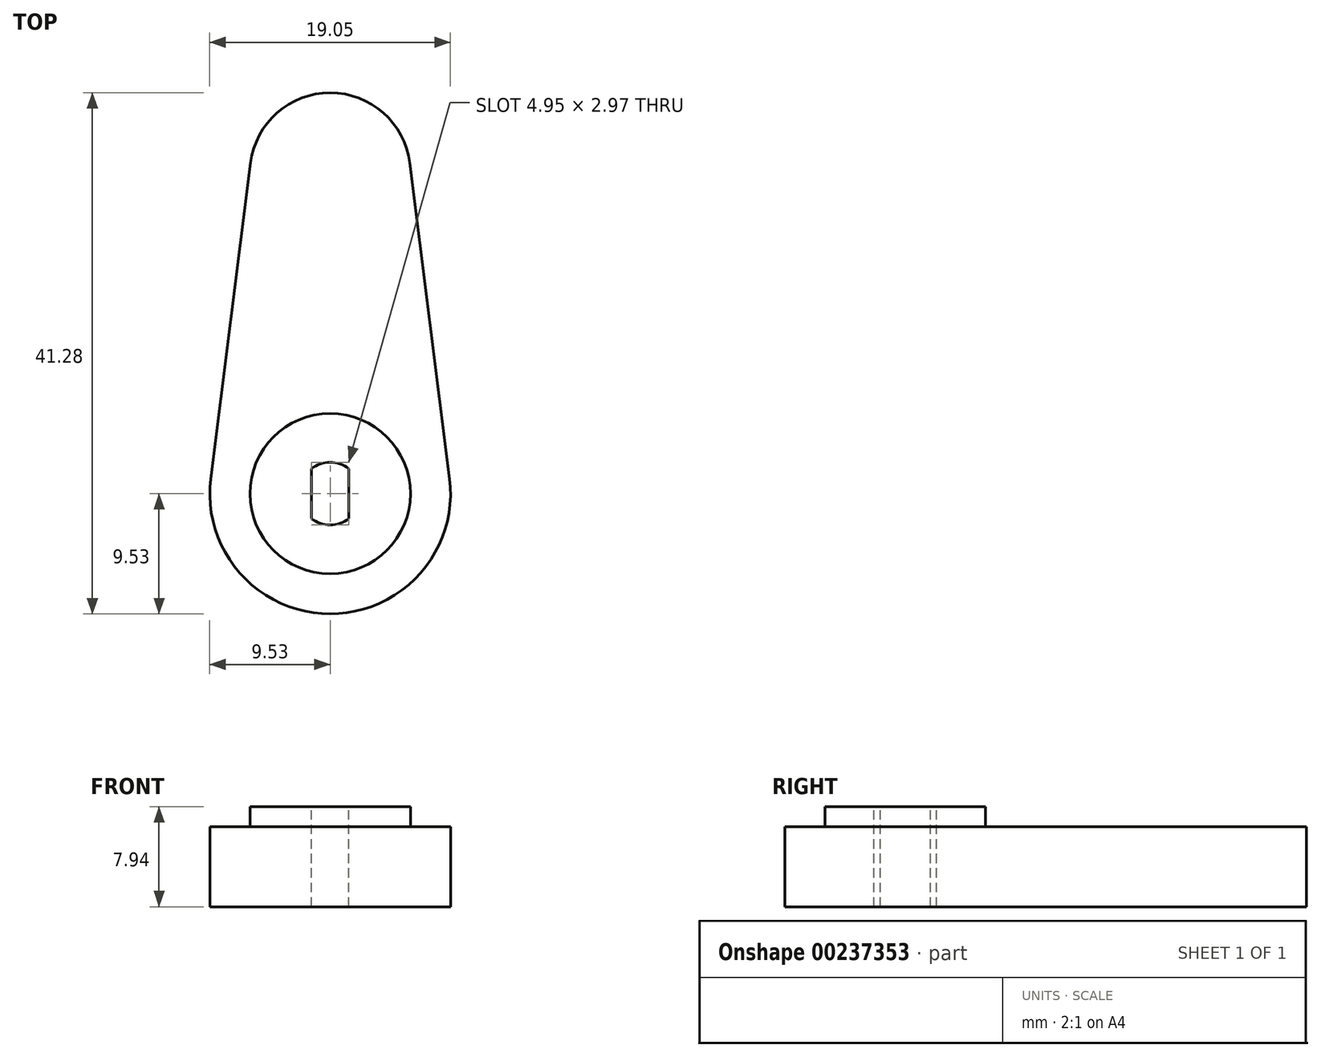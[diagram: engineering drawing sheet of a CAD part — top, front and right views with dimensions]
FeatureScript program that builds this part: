
annotation { "Feature Type Name" : "Feature", "Feature Type Description" : "" }
export const myFeature = defineFeature(function(context is Context, id is Id, definition is map)
    precondition{}
    {
        {
            var Q0;
            Q0=qCreatedBy(makeId("Top.planeOp"),FACE);
            var sketch = newSketch(context, id + "F0", { "sketchPlane" : qUnion([Q0])});
            skArc(sketch, "E0", {"start": v(-1.49, -1.98) * mm, "mid": v(0, -2.48) * mm, "end": v(1.49, -1.98) * mm});
            skLineSegment(sketch, "E1", {"start": v(-1.49, -1.98) * mm, "end": v(-1.49, 1.98) * mm});
            skLineSegment(sketch, "E2", {"start": v(1.49, -1.98) * mm, "end": v(1.49, 1.98) * mm});
            skArc(sketch, "E3.trimOffspring", {"start": v(1.49, 1.98) * mm, "mid": v(0, 2.48) * mm, "end": v(-1.49, 1.98) * mm});
            skPoint(sketch, "E4.orphan", {"position": v(1.49, 5.26) * mm});
            skPoint(sketch, "E5.orphan", {"position": v(-1.49, 5.26) * mm});
            skPoint(sketch, "E6.orphan", {"position": v(-1.49, -3.31) * mm});
            skCircle(sketch, "E7", {"center": v(0, 0) * mm, "radius": 6.35 * mm});
            skSolve(sketch);
        }
        {
            var Q0;
            Q0=makeQuery(id+"F0.imprint","IMPRINT",FACE,{"disambiguationData":[TD([[makeQuery(id+"F0.imprint","IMPRINT",EDGE,{"derivedFrom":sQuery(id+"F0.wireOp",EDGE,"E0")}),-1.0]])]});
            extrude(context, id + "F1", {"entities" : qUnion([Q0]), "oppositeDirection" : true, "depth" : 1.59 * mm});
        }
        {
            var Q0;
            Q0=makeQuery(id+"F1.opExtrude","CAP_FACE",FACE,{"disambiguationData":[OSD([sQuery(id+"F0.wireOp",EDGE,"E0"),sQuery(id+"F0.wireOp",EDGE,"E1"),sQuery(id+"F0.wireOp",EDGE,"E2"),sQuery(id+"F0.wireOp",EDGE,"E3.trimOffspring"),sQuery(id+"F0.wireOp",EDGE,"E7")])],"isStart":false});
            var sketch = newSketch(context, id + "F2", { "sketchPlane" : qUnion([Q0])});
            skArc(sketch, "E8", {"start": v(9.45, -1.2) * mm, "mid": v(0, 9.52) * mm, "end": v(-9.45, -1.2) * mm});
            skArc(sketch, "E9", {"start": v(-6.3, -26.2) * mm, "mid": v(0, -31.75) * mm, "end": v(6.3, -26.2) * mm});
            skLineSegment(sketch, "E10", {"start": v(6.3, -26.2) * mm, "end": v(9.45, -1.2) * mm});
            skLineSegment(sketch, "E11", {"start": v(-9.45, -1.2) * mm, "end": v(-6.3, -26.2) * mm});
            skSolve(sketch);
        }
        {
            var Q0;
            Q0=makeQuery(id+"F2.imprint","IMPRINT",FACE,{"disambiguationData":[TD([[makeQuery(id+"F2.imprint","IMPRINT",EDGE,{"derivedFrom":makeQuery(id+"F1.opExtrude","CAP_EDGE",EDGE,{"disambiguationData":[OSD([sQuery(id+"F0.wireOp",EDGE,"E0")])],"isStart":false})}),1.0]])]});
            var Q1;
            Q1=makeQuery(id+"F2.imprint","IMPRINT",FACE,{"disambiguationData":[TD([[makeQuery(id+"F2.imprint","IMPRINT",EDGE,{"derivedFrom":sQuery(id+"F2.wireOp",EDGE,"E8")}),1.0]])]});
            extrude(context, id + "F3", {"entities" : qUnion([Q0, Q1]), "operationType" : NewBodyOperationType.ADD, "depth" : 6.35 * mm});
        }
    });
